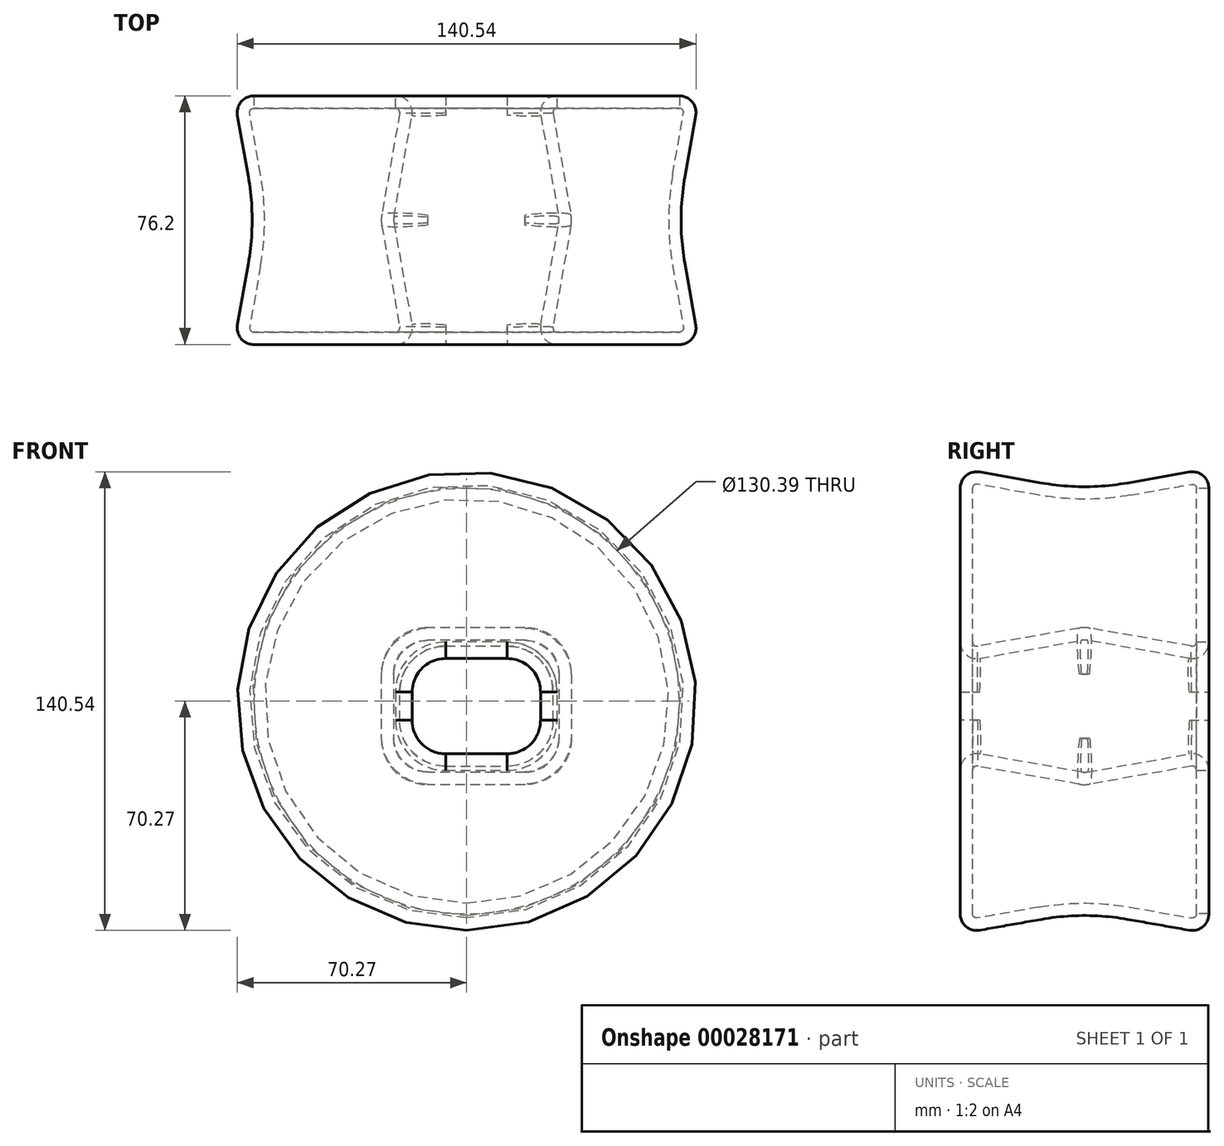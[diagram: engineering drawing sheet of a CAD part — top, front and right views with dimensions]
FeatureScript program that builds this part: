
annotation { "Feature Type Name" : "Feature", "Feature Type Description" : "" }
export const myFeature = defineFeature(function(context is Context, id is Id, definition is map)
    precondition{}
    {
        {
            var Q0;
            Q0=qCreatedBy(makeId("Front.planeOp"),FACE);
            var sketch = newSketch(context, id + "F0", { "sketchPlane" : qUnion([Q0])});
            skCircle(sketch, "E0", {"center": v(0, 0) * mm, "radius": 64.53 * mm});
            skLineSegment(sketch, "E1.bottom", {"start": v(-22.41, -21.86) * mm, "end": v(28.39, -21.86) * mm});
            skLineSegment(sketch, "E1.top", {"start": v(-22.41, 18.78) * mm, "end": v(28.39, 18.78) * mm});
            skLineSegment(sketch, "E1.left", {"start": v(-22.41, -21.86) * mm, "end": v(-22.41, 18.78) * mm});
            skLineSegment(sketch, "E1.right", {"start": v(28.39, -21.86) * mm, "end": v(28.39, 18.78) * mm});
            skSolve(sketch);
        }
        {
            var Q0;
            Q0=makeQuery(id+"F0.imprint","IMPRINT",FACE,{"disambiguationData":[TD([[makeQuery(id+"F0.imprint","IMPRINT",EDGE,{"derivedFrom":sQuery(id+"F0.wireOp",EDGE,"E0")}),1.0]])]});
            extrude(context, id + "F1", {"entities" : qUnion([Q0]), "endBound" : BoundingType.SYMMETRIC, "depth" : 76.2 * mm, "hasDraft" : true, "draftAngle" : 10 * degree});
        }
        {
            var Q0;
            Q0=makeQuery(id+"F1.opExtrude","CAP_EDGE",EDGE,{"disambiguationData":[OSD([sQuery(id+"F0.wireOp",EDGE,"E0")])],"isStart":true});
            var Q1;
            Q1=makeQuery(id+"F1.opExtrude","CAP_EDGE",EDGE,{"disambiguationData":[OSD([sQuery(id+"F0.wireOp",EDGE,"E0")])],"isStart":false});
            fillet(context, id + "F2", {"entities" : qUnion([Q0, Q1]), "radius" : 5.08 * mm, "tangentPropagation" : true, "allowEdgeOverflow" : false});
        }
        {
            var Q0;
            {var subQ0=makeQuery(id+"F1.opExtrude","SWEPT_FACE",FACE,{"disambiguationData":[OSD([sQuery(id+"F0.wireOp",EDGE,"E0")])]});Q0=makeQuery(id+"F1.*.booleanUnion.opBoolean","MERGE",EDGE,{"derivedFrom":[makeQuery(id+"F1.*.split.splitOp","SPLIT_SURFACE_INTERSECT",EDGE,{"derivedFrom":[subQ0]}),makeQuery(id+"F1.*.split.splitOp","SPLIT_SURFACE_INTERSECT",EDGE,{"derivedFrom":[subQ0],"isFromBackBody":true})]});}
            fillet(context, id + "F3", {"entities" : qUnion([Q0]), "radius" : 76.2 * mm, "tangentPropagation" : true, "allowEdgeOverflow" : false});
        }
        {
            var Q0;
            Q0=makeQuery(id+"F1.*.split.splitOp","SPLIT",EDGE,{"derivedFrom":makeQuery(id+"F1.opExtrude","SWEPT_EDGE",EDGE,{"disambiguationData":[OSD([sQuery(id+"F0.wireOp",EDGE,"E1.top"),sQuery(id+"F0.wireOp",EDGE,"E1.right")])]})});
            var Q1;
            Q1=makeQuery(id+"F1.*.split.splitOp","SPLIT",EDGE,{"derivedFrom":makeQuery(id+"F1.opExtrude","SWEPT_EDGE",EDGE,{"disambiguationData":[OSD([sQuery(id+"F0.wireOp",EDGE,"E1.top"),sQuery(id+"F0.wireOp",EDGE,"E1.right")])]}),"isFromBackBody":true});
            var Q2;
            Q2=makeQuery(id+"F1.*.split.splitOp","SPLIT",EDGE,{"derivedFrom":makeQuery(id+"F1.opExtrude","SWEPT_EDGE",EDGE,{"disambiguationData":[OSD([sQuery(id+"F0.wireOp",EDGE,"E1.top"),sQuery(id+"F0.wireOp",EDGE,"E1.left")])]})});
            var Q3;
            Q3=makeQuery(id+"F1.*.split.splitOp","SPLIT",EDGE,{"derivedFrom":makeQuery(id+"F1.opExtrude","SWEPT_EDGE",EDGE,{"disambiguationData":[OSD([sQuery(id+"F0.wireOp",EDGE,"E1.top"),sQuery(id+"F0.wireOp",EDGE,"E1.left")])]}),"isFromBackBody":true});
            var Q4;
            Q4=makeQuery(id+"F1.*.split.splitOp","SPLIT",EDGE,{"derivedFrom":makeQuery(id+"F1.opExtrude","SWEPT_EDGE",EDGE,{"disambiguationData":[OSD([sQuery(id+"F0.wireOp",EDGE,"E1.bottom"),sQuery(id+"F0.wireOp",EDGE,"E1.left")])]})});
            var Q5;
            Q5=makeQuery(id+"F1.*.split.splitOp","SPLIT",EDGE,{"derivedFrom":makeQuery(id+"F1.opExtrude","SWEPT_EDGE",EDGE,{"disambiguationData":[OSD([sQuery(id+"F0.wireOp",EDGE,"E1.bottom"),sQuery(id+"F0.wireOp",EDGE,"E1.left")])]}),"isFromBackBody":true});
            var Q6;
            Q6=makeQuery(id+"F1.*.split.splitOp","SPLIT",EDGE,{"derivedFrom":makeQuery(id+"F1.opExtrude","SWEPT_EDGE",EDGE,{"disambiguationData":[OSD([sQuery(id+"F0.wireOp",EDGE,"E1.bottom"),sQuery(id+"F0.wireOp",EDGE,"E1.right")])]}),"isFromBackBody":true});
            var Q7;
            Q7=makeQuery(id+"F1.*.split.splitOp","SPLIT",EDGE,{"derivedFrom":makeQuery(id+"F1.opExtrude","SWEPT_EDGE",EDGE,{"disambiguationData":[OSD([sQuery(id+"F0.wireOp",EDGE,"E1.bottom"),sQuery(id+"F0.wireOp",EDGE,"E1.right")])]})});
            fillet(context, id + "F4", {"entities" : qUnion([Q0, Q1, Q2, Q3, Q4, Q5, Q6, Q7]), "radius" : 10.48 * mm, "tangentPropagation" : true, "allowEdgeOverflow" : false});
        }
        {
            var Q0;
            {var subQ0=makeQuery(id+"F1.opExtrude","SWEPT_FACE",FACE,{"disambiguationData":[OSD([sQuery(id+"F0.wireOp",EDGE,"E1.bottom")])]});Q0=makeQuery(id+"F1.*.booleanUnion.opBoolean","MERGE",EDGE,{"derivedFrom":[makeQuery(id+"F1.*.split.splitOp","SPLIT_SURFACE_INTERSECT",EDGE,{"derivedFrom":[subQ0]}),makeQuery(id+"F1.*.split.splitOp","SPLIT_SURFACE_INTERSECT",EDGE,{"derivedFrom":[subQ0],"isFromBackBody":true})]});}
            var Q1;
            {var subQ0=makeQuery(id+"F1.opExtrude","SWEPT_EDGE",EDGE,{"disambiguationData":[OSD([sQuery(id+"F0.wireOp",EDGE,"E1.bottom"),sQuery(id+"F0.wireOp",EDGE,"E1.left")])]});Q1=makeQuery(id+"F4.opFillet","BLEND_EDGE",EDGE,{"blendedFrom":[makeQuery(id+"F1.*.split.splitOp","SPLIT",EDGE,{"derivedFrom":subQ0,"isFromBackBody":true}),makeQuery(id+"F1.*.split.splitOp","SPLIT",EDGE,{"derivedFrom":subQ0})],"blendedInto":[]});}
            var Q2;
            {var subQ0=makeQuery(id+"F1.opExtrude","SWEPT_FACE",FACE,{"disambiguationData":[OSD([sQuery(id+"F0.wireOp",EDGE,"E1.left")])]});Q2=makeQuery(id+"F1.*.booleanUnion.opBoolean","MERGE",EDGE,{"derivedFrom":[makeQuery(id+"F1.*.split.splitOp","SPLIT_SURFACE_INTERSECT",EDGE,{"derivedFrom":[subQ0]}),makeQuery(id+"F1.*.split.splitOp","SPLIT_SURFACE_INTERSECT",EDGE,{"derivedFrom":[subQ0],"isFromBackBody":true})]});}
            var Q3;
            {var subQ0=makeQuery(id+"F1.opExtrude","SWEPT_EDGE",EDGE,{"disambiguationData":[OSD([sQuery(id+"F0.wireOp",EDGE,"E1.top"),sQuery(id+"F0.wireOp",EDGE,"E1.left")])]});Q3=makeQuery(id+"F4.opFillet","BLEND_EDGE",EDGE,{"blendedFrom":[makeQuery(id+"F1.*.split.splitOp","SPLIT",EDGE,{"derivedFrom":subQ0,"isFromBackBody":true}),makeQuery(id+"F1.*.split.splitOp","SPLIT",EDGE,{"derivedFrom":subQ0})],"blendedInto":[]});}
            var Q4;
            {var subQ0=makeQuery(id+"F1.opExtrude","SWEPT_FACE",FACE,{"disambiguationData":[OSD([sQuery(id+"F0.wireOp",EDGE,"E1.top")])]});Q4=makeQuery(id+"F1.*.booleanUnion.opBoolean","MERGE",EDGE,{"derivedFrom":[makeQuery(id+"F1.*.split.splitOp","SPLIT_SURFACE_INTERSECT",EDGE,{"derivedFrom":[subQ0]}),makeQuery(id+"F1.*.split.splitOp","SPLIT_SURFACE_INTERSECT",EDGE,{"derivedFrom":[subQ0],"isFromBackBody":true})]});}
            var Q5;
            {var subQ0=makeQuery(id+"F1.opExtrude","SWEPT_EDGE",EDGE,{"disambiguationData":[OSD([sQuery(id+"F0.wireOp",EDGE,"E1.top"),sQuery(id+"F0.wireOp",EDGE,"E1.right")])]});Q5=makeQuery(id+"F4.opFillet","BLEND_EDGE",EDGE,{"blendedFrom":[makeQuery(id+"F1.*.split.splitOp","SPLIT",EDGE,{"derivedFrom":subQ0,"isFromBackBody":true}),makeQuery(id+"F1.*.split.splitOp","SPLIT",EDGE,{"derivedFrom":subQ0})],"blendedInto":[]});}
            var Q6;
            {var subQ0=makeQuery(id+"F1.opExtrude","SWEPT_FACE",FACE,{"disambiguationData":[OSD([sQuery(id+"F0.wireOp",EDGE,"E1.right")])]});Q6=makeQuery(id+"F1.*.booleanUnion.opBoolean","MERGE",EDGE,{"derivedFrom":[makeQuery(id+"F1.*.split.splitOp","SPLIT_SURFACE_INTERSECT",EDGE,{"derivedFrom":[subQ0]}),makeQuery(id+"F1.*.split.splitOp","SPLIT_SURFACE_INTERSECT",EDGE,{"derivedFrom":[subQ0],"isFromBackBody":true})]});}
            var Q7;
            {var subQ0=sQuery(id+"F0.wireOp",EDGE,"E1.right");var subQ1=sQuery(id+"F0.wireOp",EDGE,"E1.bottom");Q7=makeQuery(id+"F4.opFillet","BLEND_FACE",FACE,{"disambiguationData":[OSD([subQ1,subQ0]),TDD([makeQuery(id+"F1.*.split.splitOp","SPLIT",EDGE,{"derivedFrom":makeQuery(id+"F1.opExtrude","SWEPT_EDGE",EDGE,{"disambiguationData":[OSD([subQ1,subQ0])]})})])]});}
            var Q8;
            {var subQ0=makeQuery(id+"F1.opExtrude","SWEPT_EDGE",EDGE,{"disambiguationData":[OSD([sQuery(id+"F0.wireOp",EDGE,"E1.bottom"),sQuery(id+"F0.wireOp",EDGE,"E1.right")])]});Q8=makeQuery(id+"F4.opFillet","BLEND_EDGE",EDGE,{"blendedFrom":[makeQuery(id+"F1.*.split.splitOp","SPLIT",EDGE,{"derivedFrom":subQ0,"isFromBackBody":true}),makeQuery(id+"F1.*.split.splitOp","SPLIT",EDGE,{"derivedFrom":subQ0})],"blendedInto":[]});}
            fillet(context, id + "F5", {"entities" : qUnion([Q0, Q1, Q2, Q3, Q4, Q5, Q6, Q7, Q8]), "radius" : 5.08 * mm, "tangentPropagation" : true, "allowEdgeOverflow" : false});
        }
        {
            var Q0;
            Q0=makeQuery(id+"F1.opExtrude","CAP_EDGE",EDGE,{"disambiguationData":[OSD([sQuery(id+"F0.wireOp",EDGE,"E1.bottom")])],"isStart":true});
            fillet(context, id + "F6", {"entities" : qUnion([Q0]), "radius" : 5.08 * mm, "tangentPropagation" : true, "allowEdgeOverflow" : false});
        }
        {
            var Q0;
            Q0=makeQuery(id+"F1.opExtrude","CAP_FACE",FACE,{"disambiguationData":[OSD([sQuery(id+"F0.wireOp",EDGE,"E0"),sQuery(id+"F0.wireOp",EDGE,"E1.bottom"),sQuery(id+"F0.wireOp",EDGE,"E1.top"),sQuery(id+"F0.wireOp",EDGE,"E1.left"),sQuery(id+"F0.wireOp",EDGE,"E1.right")])],"isStart":true});
            shell(context, id + "F7", {"entities" : qUnion([Q0]), "thickness" : 3.8 * mm});
        }
    });
